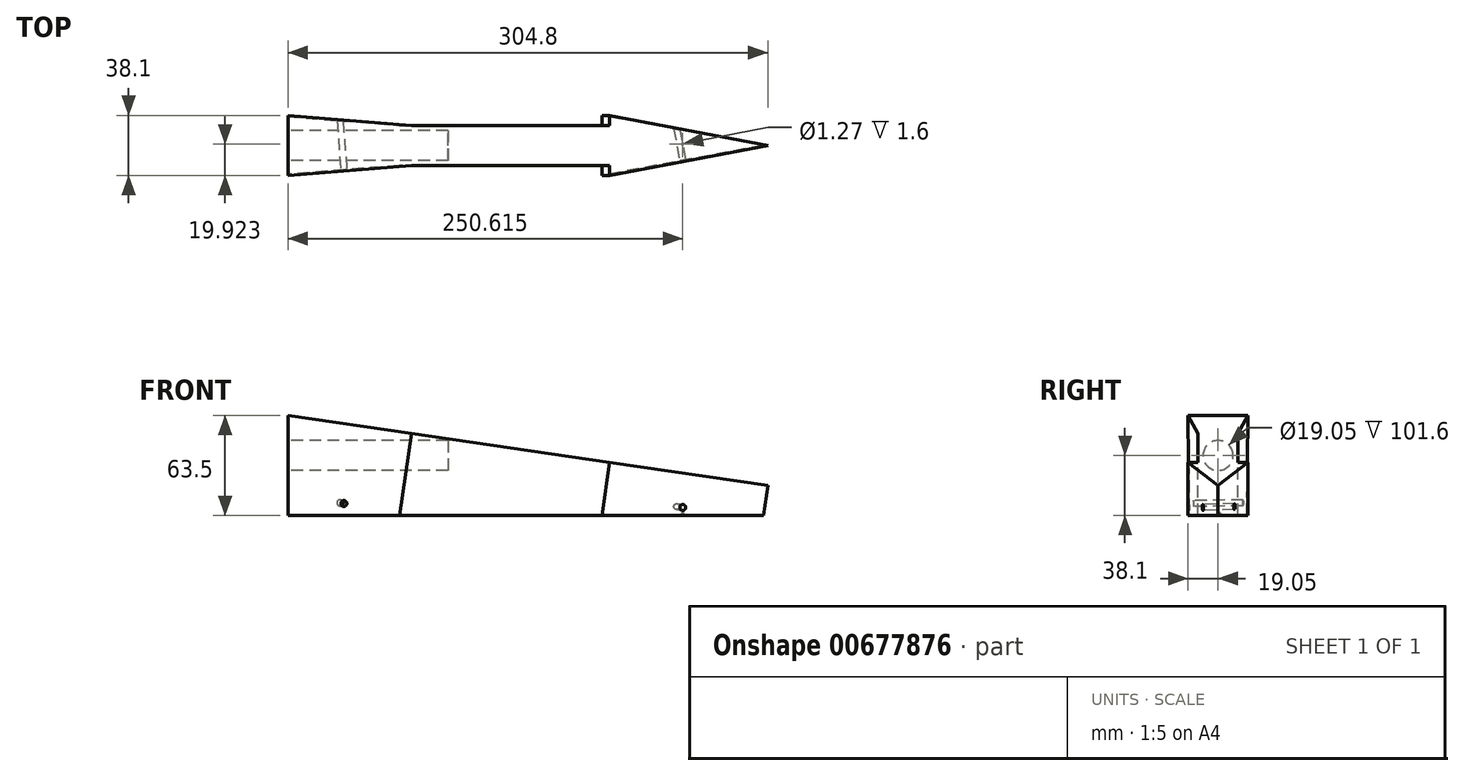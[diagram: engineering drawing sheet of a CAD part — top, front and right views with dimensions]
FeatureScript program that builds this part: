
annotation { "Feature Type Name" : "Feature", "Feature Type Description" : "" }
export const myFeature = defineFeature(function(context is Context, id is Id, definition is map)
    precondition{}
    {
        {
            var Q0;
            Q0=qCreatedBy(makeId("Front.planeOp"),FACE);
            var sketch = newSketch(context, id + "F0", { "sketchPlane" : qUnion([Q0])});
            skLineSegment(sketch, "E0", {"start": v(0, 0) * mm, "end": v(304.8, 0) * mm});
            skLineSegment(sketch, "E1", {"start": v(304.8, 0) * mm, "end": v(304.8, 19.05) * mm});
            skLineSegment(sketch, "E2", {"start": v(0, 0) * mm, "end": v(0, 63.5) * mm});
            skLineSegment(sketch, "E3", {"start": v(0, 63.5) * mm, "end": v(304.8, 19.05) * mm});
            skSolve(sketch);
        }
        {
            var Q0;
            Q0=makeQuery(id+"F0.imprint","IMPRINT",FACE,{"disambiguationData":[TD([[makeQuery(id+"F0.imprint","IMPRINT",EDGE,{"derivedFrom":sQuery(id+"F0.wireOp",EDGE,"E0")}),1.0]])]});
            extrude(context, id + "F1", {"entities" : qUnion([Q0]), "depth" : 38.1 * mm, "offsetDistance" : 25.4 * mm});
        }
        {
            var Q0;
            Q0=makeQuery(id+"F1.opExtrude","SWEPT_FACE",FACE,{"disambiguationData":[OSD([sQuery(id+"F0.wireOp",EDGE,"E2")])]});
            var sketch = newSketch(context, id + "F2", { "sketchPlane" : qUnion([Q0])});
            skCircle(sketch, "E4", {"center": v(19.05, 38.1) * mm, "radius": 9.53 * mm});
            skSolve(sketch);
        }
        {
            var Q0;
            Q0 = qSketchRegion(id + "F2", true);
            extrude(context, id + "F3", {"entities" : qUnion([Q0]), "operationType" : NewBodyOperationType.REMOVE, "oppositeDirection" : true, "depth" : 101.6 * mm, "offsetDistance" : 25.4 * mm});
        }
        {
            var Q0;
            Q0=makeQuery(id+"F1.opExtrude","SWEPT_FACE",FACE,{"disambiguationData":[OSD([sQuery(id+"F0.wireOp",EDGE,"E3")])]});
            var sketch = newSketch(context, id + "F4", { "sketchPlane" : qUnion([Q0])});
            skLineSegment(sketch, "E5", {"start": v(298.86, 0) * mm, "end": v(197.26, 0) * mm});
            skLineSegment(sketch, "E6", {"start": v(298.86, -38.1) * mm, "end": v(197.26, -38.1) * mm});
            skLineSegment(sketch, "E7", {"start": v(298.86, -19.05) * mm, "end": v(197.26, 0) * mm});
            skLineSegment(sketch, "E8", {"start": v(298.86, -19.05) * mm, "end": v(197.26, -38.1) * mm});
            skLineSegment(sketch, "E9", {"start": v(197.26, 0) * mm, "end": v(197.26, -6.35) * mm});
            skLineSegment(sketch, "E10", {"start": v(197.26, -38.1) * mm, "end": v(197.26, -31.75) * mm});
            skLineSegment(sketch, "E11", {"start": v(197.26, -31.75) * mm, "end": v(95.66, -31.75) * mm});
            skLineSegment(sketch, "E12", {"start": v(197.26, -6.35) * mm, "end": v(95.66, -6.35) * mm});
            skLineSegment(sketch, "E13", {"start": v(95.66, -6.35) * mm, "end": v(70.26, -6.35) * mm});
            skLineSegment(sketch, "E14", {"start": v(95.66, -31.75) * mm, "end": v(70.26, -31.75) * mm});
            skLineSegment(sketch, "E15", {"start": v(70.26, -31.75) * mm, "end": v(-9.16, -38.1) * mm});
            skLineSegment(sketch, "E16", {"start": v(-9.16, -38.1) * mm, "end": v(-9.16, 0) * mm});
            skLineSegment(sketch, "E17", {"start": v(-9.16, 0) * mm, "end": v(70.26, -6.35) * mm});
            skSolve(sketch);
        }
        {
            var Q0;
            {var subQ1=sQuery(id+"F4.wireOp",EDGE,"E9");Q0=makeQuery(id+"F4.imprint","IMPRINT",FACE,{"disambiguationData":[TD([[makeQuery(id+"F4.imprint","IMPRINT",EDGE,{"derivedFrom":subQ1}),-1.0]])]});}
            var Q1;
            {var subQ1=sQuery(id+"F4.wireOp",EDGE,"E10");Q1=makeQuery(id+"F4.imprint","IMPRINT",FACE,{"disambiguationData":[TD([[makeQuery(id+"F4.imprint","IMPRINT",EDGE,{"derivedFrom":subQ1}),1.0]])]});}
            var Q2;
            {var subQ0=sQuery(id+"F4.wireOp",EDGE,"E5");Q2=makeQuery(id+"F4.imprint","IMPRINT",FACE,{"disambiguationData":[TD([[makeQuery(id+"F4.imprint","IMPRINT",EDGE,{"derivedFrom":subQ0}),-1.0]])]});}
            var Q3;
            {var subQ0=sQuery(id+"F4.wireOp",EDGE,"E6");Q3=makeQuery(id+"F4.imprint","IMPRINT",FACE,{"disambiguationData":[TD([[makeQuery(id+"F4.imprint","IMPRINT",EDGE,{"derivedFrom":subQ0}),1.0]])]});}
            var Q4;
            Q4=makeQuery(id+"F1.opExtrude","SWEPT_FACE",FACE,{"disambiguationData":[OSD([sQuery(id+"F0.wireOp",EDGE,"E1")])]});
            extrude(context, id + "F5", {"entities" : qUnion([Q0, Q1, Q2, Q3, Q4]), "operationType" : NewBodyOperationType.REMOVE, "oppositeDirection" : true, "depth" : 152.4 * mm, "offsetDistance" : 25.4 * mm});
        }
        {
            var Q0;
            Q0=makeQuery(id+"F5.boolean.opBoolean","COPY",FACE,{"derivedFrom":makeQuery(id+"F5.opExtrude","SWEPT_FACE",FACE,{"disambiguationData":[OSD([sQuery(id+"F4.wireOp",EDGE,"E15")])]})});
            var sketch = newSketch(context, id + "F6", { "sketchPlane" : qUnion([Q0])});
            skLineSegment(sketch, "E18", {"start": v(32.67, 0.4) * mm, "end": v(32.67, 8.02) * mm});
            skCircle(sketch, "E19", {"center": v(32.67, 8.02) * mm, "radius": 1.9 * mm});
            skSolve(sketch);
        }
        {
            var Q0;
            Q0=makeQuery(id+"F6.imprint","IMPRINT",FACE,{"disambiguationData":[TD([[makeQuery(id+"F6.imprint","IMPRINT",EDGE,{"derivedFrom":sQuery(id+"F6.wireOp",EDGE,"E19")}),1.0]])]});
            extrude(context, id + "F7", {"entities" : qUnion([Q0]), "operationType" : NewBodyOperationType.REMOVE, "oppositeDirection" : true, "depth" : 63.5 * mm, "offsetDistance" : 25.4 * mm});
        }
        {
            var Q0;
            Q0=makeQuery(id+"F5.boolean.opBoolean","COPY",FACE,{"derivedFrom":makeQuery(id+"F5.opExtrude","SWEPT_FACE",FACE,{"disambiguationData":[OSD([sQuery(id+"F4.wireOp",EDGE,"E8")])]})});
            var sketch = newSketch(context, id + "F8", { "sketchPlane" : qUnion([Q0])});
            skLineSegment(sketch, "E20", {"start": v(241.27, 0.77) * mm, "end": v(241.3, 5.85) * mm});
            skCircle(sketch, "E21", {"center": v(241.3, 5.85) * mm, "radius": 1.9 * mm});
            skSolve(sketch);
        }
        {
            var Q0;
            Q0 = qSketchRegion(id + "F8", true);
            extrude(context, id + "F9", {"entities" : qUnion([Q0]), "operationType" : NewBodyOperationType.REMOVE, "oppositeDirection" : true, "depth" : 50.8 * mm, "offsetDistance" : 25.4 * mm});
        }
        {
            var Q0;
            Q0=makeQuery(id+"F1.opExtrude","SWEPT_FACE",FACE,{"disambiguationData":[OSD([sQuery(id+"F0.wireOp",EDGE,"E0")])]});
            var sketch = newSketch(context, id + "F10", { "sketchPlane" : qUnion([Q0])});
            skCircle(sketch, "E22", {"center": v(250.62, 18.18) * mm, "radius": 0.64 * mm});
            skSolve(sketch);
        }
        {
            var Q0;
            Q0=makeQuery(id+"F10.imprint","IMPRINT",FACE,{"disambiguationData":[TD([[makeQuery(id+"F10.imprint","IMPRINT",EDGE,{"derivedFrom":sQuery(id+"F10.wireOp",EDGE,"E22")}),1.0]])]});
            extrude(context, id + "F11", {"entities" : qUnion([Q0]), "operationType" : NewBodyOperationType.REMOVE, "oppositeDirection" : true, "depth" : 1.6 * mm, "offsetDistance" : 25.4 * mm});
        }
    });
